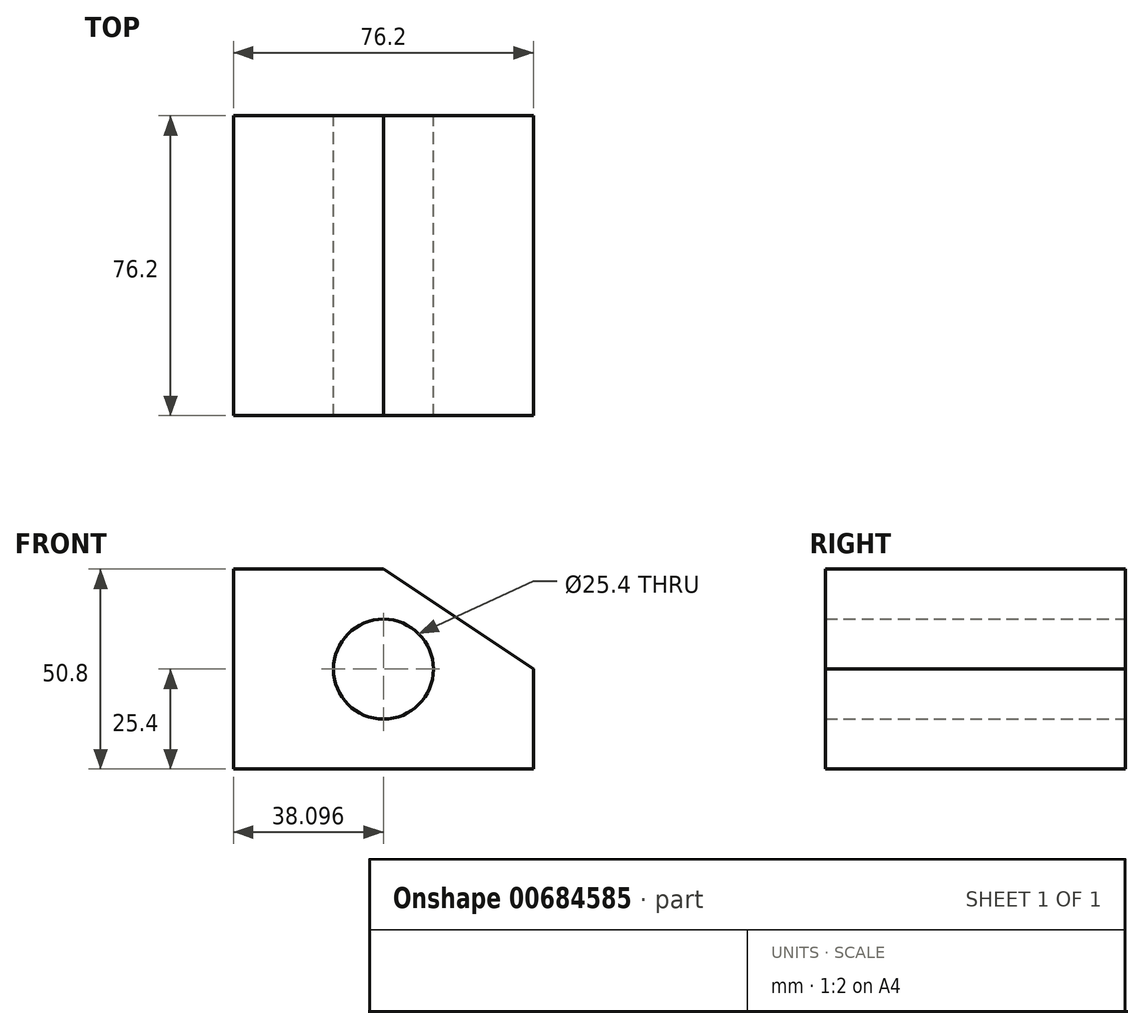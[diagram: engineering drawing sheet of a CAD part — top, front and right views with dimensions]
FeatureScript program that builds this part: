
annotation { "Feature Type Name" : "Feature", "Feature Type Description" : "" }
export const myFeature = defineFeature(function(context is Context, id is Id, definition is map)
    precondition{}
    {
        {
            var Q0;
            Q0=qCreatedBy(makeId("Front.planeOp"),FACE);
            var sketch = newSketch(context, id + "F0", { "sketchPlane" : qUnion([Q0])});
            skLineSegment(sketch, "E0", {"start": v(-56.65, 39.6) * mm, "end": v(-56.65, -11.2) * mm});
            skLineSegment(sketch, "E1", {"start": v(-56.65, -11.2) * mm, "end": v(19.55, -11.2) * mm});
            skLineSegment(sketch, "E2", {"start": v(-56.65, 39.6) * mm, "end": v(-18.55, 39.6) * mm});
            skLineSegment(sketch, "E3", {"start": v(19.55, -11.2) * mm, "end": v(19.55, 14.2) * mm});
            skLineSegment(sketch, "E4", {"start": v(-18.55, 39.6) * mm, "end": v(19.55, 14.2) * mm});
            skPoint(sketch, "E5.positionSnap0", {"position": v(-56.65, 14.2) * mm});
            skPoint(sketch, "E6", {"position": v(-18.55, 14.2) * mm});
            skCircle(sketch, "E7", {"center": v(-18.55, 14.2) * mm, "radius": 12.7 * mm});
            skSolve(sketch);
        }
        {
            var Q0;
            Q0=qCreatedBy(makeId("Front.planeOp"),FACE);
            var sketch = newSketch(context, id + "F1", { "sketchPlane" : qUnion([Q0])});
            skLineSegment(sketch, "E8", {"start": v(-65.46, 47.8) * mm, "end": v(-54.46, 47.8) * mm});
            skLineSegment(sketch, "E9", {"start": v(-65.46, 47.8) * mm, "end": v(-65.46, -4.33) * mm});
            skLineSegment(sketch, "E10", {"start": v(-42.43, 47.8) * mm, "end": v(-31.43, 47.8) * mm});
            skLineSegment(sketch, "E11", {"start": v(-31.43, 47.8) * mm, "end": v(-31.43, -4.2) * mm});
            skLineSegment(sketch, "E12", {"start": v(-54.46, 47.8) * mm, "end": v(-54.46, 5.8) * mm});
            skLineSegment(sketch, "E13", {"start": v(-42.43, 47.8) * mm, "end": v(-42.43, 5.8) * mm});
            skSolve(sketch);
        }
        {
            var Q0;
            Q0=makeQuery(id+"F0.imprint","IMPRINT",FACE,{"disambiguationData":[TD([[makeQuery(id+"F0.imprint","IMPRINT",EDGE,{"derivedFrom":sQuery(id+"F0.wireOp",EDGE,"E0")}),1.0]])]});
            var Q1;
            Q1 = qSketchRegion(id + "F1", true);
            extrude(context, id + "F2", {"entities" : qUnion([Q0, Q1]), "depth" : 76.2 * mm, "offsetDistance" : 25.4 * mm});
        }
    });
